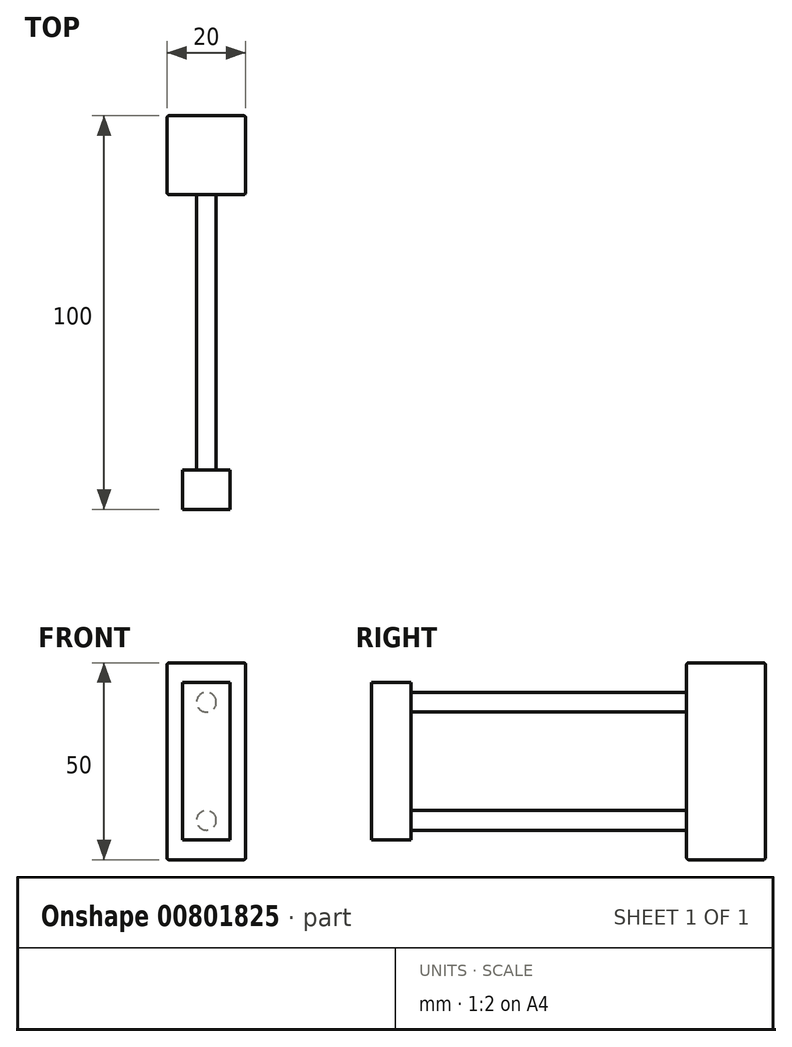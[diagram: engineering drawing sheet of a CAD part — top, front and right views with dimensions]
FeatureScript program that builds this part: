
annotation { "Feature Type Name" : "Feature", "Feature Type Description" : "" }
export const myFeature = defineFeature(function(context is Context, id is Id, definition is map)
    precondition{}
    {
        {
            var Q0;
            Q0=qCreatedBy(makeId("Front.planeOp"),FACE);
            var sketch = newSketch(context, id + "F0", { "sketchPlane" : qUnion([Q0])});
            skLineSegment(sketch, "E0.bottom", {"start": v(-10, 40) * mm, "end": v(10, 40) * mm});
            skLineSegment(sketch, "E0.top", {"start": v(-10, -10) * mm, "end": v(10, -10) * mm});
            skLineSegment(sketch, "E0.left", {"start": v(-10, 40) * mm, "end": v(-10, -10) * mm});
            skLineSegment(sketch, "E0.right", {"start": v(10, 40) * mm, "end": v(10, -10) * mm});
            skSolve(sketch);
        }
        {
            var Q0;
            Q0=makeQuery(id+"F0.imprint","IMPRINT",FACE,{"disambiguationData":[TD([[makeQuery(id+"F0.imprint","IMPRINT",EDGE,{"derivedFrom":sQuery(id+"F0.wireOp",EDGE,"Z7G3V4g9-uCY2-6wvC-ryna-2XNyHXx2DwvD")}),-1.0]])]});
            var Q1;
            Q1=makeQuery(id+"F0.imprint","IMPRINT",FACE,{"disambiguationData":[TD([[makeQuery(id+"F0.imprint","IMPRINT",EDGE,{"derivedFrom":sQuery(id+"F0.wireOp",EDGE,"E0.bottom")}),-1.0]])]});
            extrude(context, id + "F1", {"entities" : qUnion([Q0, Q1]), "depth" : 20 * mm, "offsetDistance" : 25 * mm});
        }
        {
            var Q0;
            Q0=makeQuery(id+"F1.opExtrude","CAP_FACE",FACE,{"disambiguationData":[OSD([sQuery(id+"F0.wireOp",EDGE,"Z7G3V4g9-uCY2-6wvC-ryna-2XNyHXx2DwvD"),sQuery(id+"F0.wireOp",EDGE,"E0.bottom"),sQuery(id+"F0.wireOp",EDGE,"E0.top"),sQuery(id+"F0.wireOp",EDGE,"E0.left"),sQuery(id+"F0.wireOp",EDGE,"E0.right"),sQuery(id+"F0.wireOp",EDGE,"OpoFQTxP-CPvV-HuCV-6MpO-msZk7k9A6E32")])],"isStart":false});
            var Q1;
            Q1=makeQuery(id+"F1.opExtrude","SWEPT_FACE",FACE,{"disambiguationData":[OSD([sQuery(id+"F0.wireOp",EDGE,"E0.right")])]});
            var Q2;
            Q2=makeQuery(id+"F1.opExtrude","SWEPT_FACE",FACE,{"disambiguationData":[OSD([sQuery(id+"F0.wireOp",EDGE,"E0.bottom")])]});
            var Q3;
            Q3=makeQuery(id+"F1.opExtrude","SWEPT_FACE",FACE,{"disambiguationData":[OSD([sQuery(id+"F0.wireOp",EDGE,"E0.left")])]});
            var Q4;
            Q4=makeQuery(id+"F1.opExtrude","CAP_FACE",FACE,{"disambiguationData":[OSD([sQuery(id+"F0.wireOp",EDGE,"Z7G3V4g9-uCY2-6wvC-ryna-2XNyHXx2DwvD"),sQuery(id+"F0.wireOp",EDGE,"E0.bottom"),sQuery(id+"F0.wireOp",EDGE,"E0.top"),sQuery(id+"F0.wireOp",EDGE,"E0.left"),sQuery(id+"F0.wireOp",EDGE,"E0.right"),sQuery(id+"F0.wireOp",EDGE,"OpoFQTxP-CPvV-HuCV-6MpO-msZk7k9A6E32")])],"isStart":true});
            var Q5;
            Q5=makeQuery(id+"F1.opExtrude","CAP_EDGE",EDGE,{"disambiguationData":[OSD([sQuery(id+"F0.wireOp",EDGE,"E0.top")])],"isStart":true});
            fillet(context, id + "F2", {"entities" : qUnion([Q0, Q1, Q2, Q3, Q4, Q5]), "radius" : 0.5 * mm, "tangentPropagation" : true, "allowEdgeOverflow" : false});
        }
        {
            var Q0;
            Q0=makeQuery(id+"F1.opExtrude","CAP_FACE",FACE,{"disambiguationData":[OSD([sQuery(id+"F0.wireOp",EDGE,"Z7G3V4g9-uCY2-6wvC-ryna-2XNyHXx2DwvD"),sQuery(id+"F0.wireOp",EDGE,"E0.bottom"),sQuery(id+"F0.wireOp",EDGE,"E0.top"),sQuery(id+"F0.wireOp",EDGE,"E0.left"),sQuery(id+"F0.wireOp",EDGE,"E0.right"),sQuery(id+"F0.wireOp",EDGE,"OpoFQTxP-CPvV-HuCV-6MpO-msZk7k9A6E32")])],"isStart":false});
            var sketch = newSketch(context, id + "F3", { "sketchPlane" : qUnion([Q0])});
            skCircle(sketch, "E1", {"center": v(0, 30) * mm, "radius": 2.5 * mm});
            skCircle(sketch, "E2", {"center": v(0, 0) * mm, "radius": 2.5 * mm});
            skSolve(sketch);
        }
        {
            var Q0;
            Q0=makeQuery(id+"F3.imprint","IMPRINT",FACE,{"disambiguationData":[TD([[makeQuery(id+"F3.imprint","IMPRINT",EDGE,{"derivedFrom":sQuery(id+"F3.wireOp",EDGE,"E1")}),1.0]])]});
            var Q1;
            Q1=makeQuery(id+"F3.imprint","IMPRINT",FACE,{"disambiguationData":[TD([[makeQuery(id+"F3.imprint","IMPRINT",EDGE,{"derivedFrom":sQuery(id+"F3.wireOp",EDGE,"E2")}),1.0]])]});
            extrude(context, id + "F4", {"entities" : qUnion([Q0, Q1]), "operationType" : NewBodyOperationType.ADD, "depth" : 70 * mm, "offsetDistance" : 25 * mm});
        }
        {
            var Q0;
            Q0=makeQuery(id+"F4.opExtrude","CAP_FACE",FACE,{"disambiguationData":[OSD([sQuery(id+"F3.wireOp",EDGE,"E1")])],"isStart":false});
            var sketch = newSketch(context, id + "F5", { "sketchPlane" : qUnion([Q0])});
            skLineSegment(sketch, "E3.bottom", {"start": v(-6, 35) * mm, "end": v(6, 35) * mm});
            skLineSegment(sketch, "E3.top", {"start": v(-6, -5) * mm, "end": v(6, -5) * mm});
            skLineSegment(sketch, "E3.left", {"start": v(-6, 35) * mm, "end": v(-6, -5) * mm});
            skLineSegment(sketch, "E3.right", {"start": v(6, 35) * mm, "end": v(6, -5) * mm});
            skCircle(sketch, "E4", {"center": v(0, 30) * mm, "radius": 2.5 * mm});
            skSolve(sketch);
        }
        {
            var Q0;
            Q0=makeQuery(id+"F5.imprint","IMPRINT",FACE,{"disambiguationData":[TD([[makeQuery(id+"F5.imprint","IMPRINT",EDGE,{"derivedFrom":sQuery(id+"F5.wireOp",EDGE,"E3.bottom")}),-1.0]])]});
            var Q1;
            Q1=makeQuery(id+"F5.imprint","IMPRINT",FACE,{"disambiguationData":[TD([[makeQuery(id+"F5.imprint","IMPRINT",EDGE,{"derivedFrom":sQuery(id+"F5.wireOp",EDGE,"E4")}),1.0]])]});
            extrude(context, id + "F6", {"entities" : qUnion([Q0, Q1]), "operationType" : NewBodyOperationType.ADD, "depth" : 10 * mm, "offsetDistance" : 25 * mm});
        }
    });
